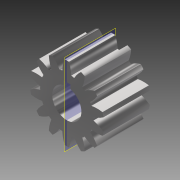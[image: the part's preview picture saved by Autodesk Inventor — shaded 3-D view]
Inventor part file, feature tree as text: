
AUTODESK INVENTOR PART (.ipt)
format: ipt  version: 2016 SP1 (Build 200210100, 210)  size: 176,640 bytes
history: native  units: in
note: dims shown in document units (in); Inventor stores cm internally (conversion verified against a paired STEP export)
features: plane x1, imported_body x1
ambient origin geometry x8: Origin, YZ Plane, XZ Plane, XY Plane, X Axis, Y Axis, Z Axis, Center Point
bodies: Solid1 (feature_tree)
feature tree (2):
  plane  "Work Plane3"
  imported_body  "Imported1"
